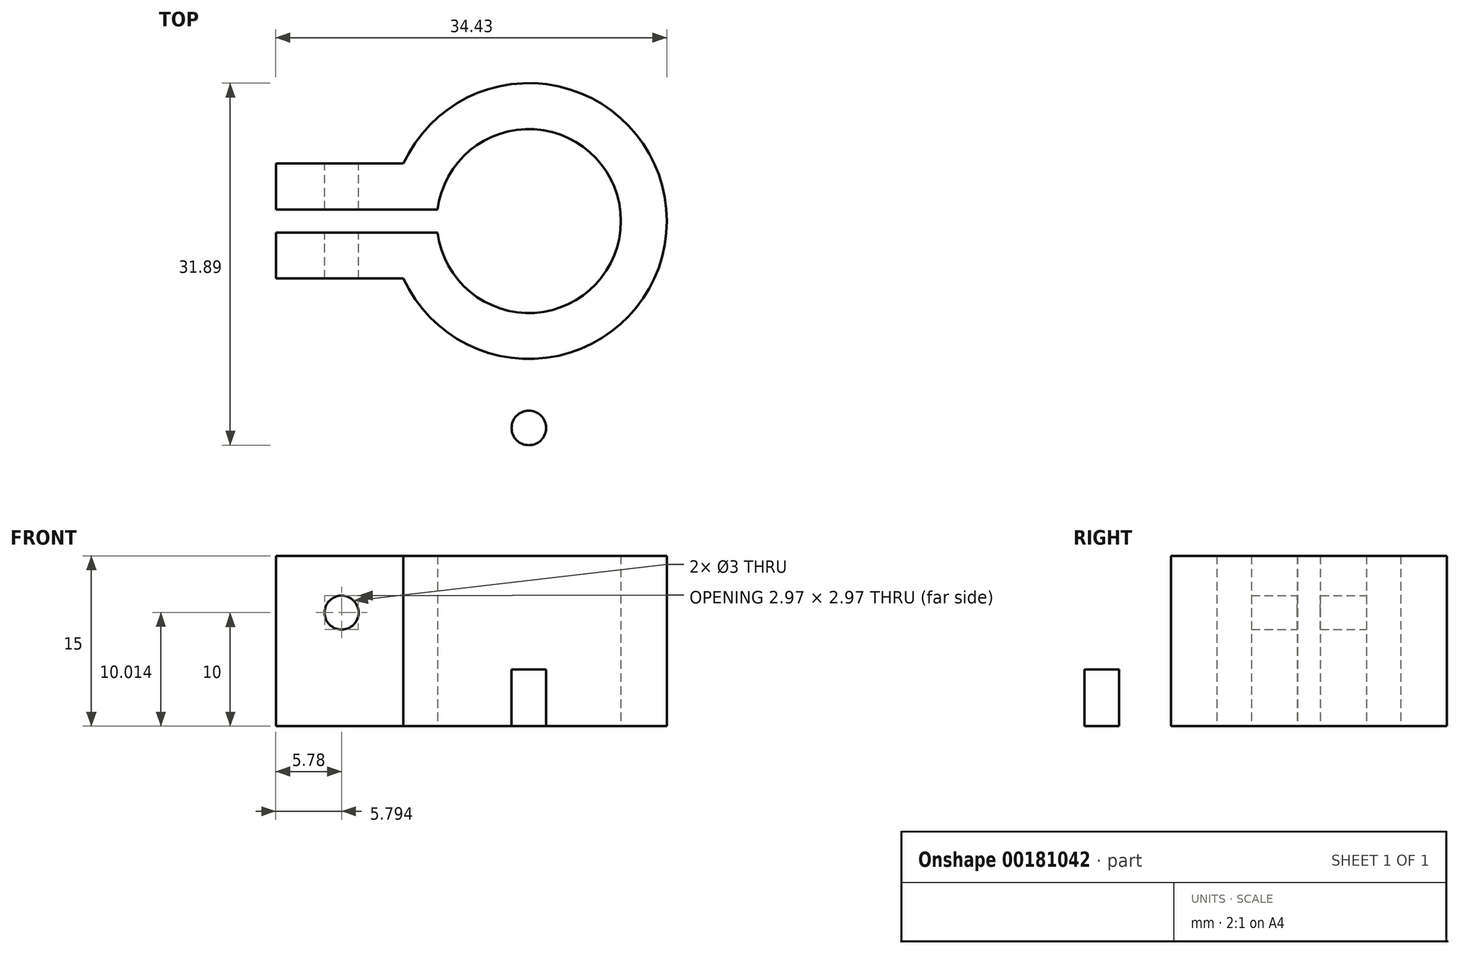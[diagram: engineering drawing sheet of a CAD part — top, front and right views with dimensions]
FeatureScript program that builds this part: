
annotation { "Feature Type Name" : "Feature", "Feature Type Description" : "" }
export const myFeature = defineFeature(function(context is Context, id is Id, definition is map)
    precondition{}
    {
        {
            var Q0;
            Q0=qCreatedBy(makeId("Top.planeOp"),FACE);
            var sketch = newSketch(context, id + "F0", { "sketchPlane" : qUnion([Q0])});
            skCircle(sketch, "E0", {"center": v(2.53, -18.82) * mm, "radius": 1.52 * mm});
            skArc(sketch, "E1", {"start": v(12.36, 17.85) * mm, "mid": v(2.53, 19.14) * mm, "end": v(-7.3, 17.85) * mm});
            skArc(sketch, "E2", {"start": v(-7.3, 17.85) * mm, "mid": v(-8.37, 16) * mm, "end": v(-6.51, 14.92) * mm});
            skArc(sketch, "E3", {"start": v(11.57, 14.92) * mm, "mid": v(2.53, 16.1) * mm, "end": v(-6.51, 14.92) * mm});
            skArc(sketch, "E4", {"start": v(11.57, 14.92) * mm, "mid": v(13.43, 16) * mm, "end": v(12.36, 17.85) * mm});
            skArc(sketch, "E5", {"start": v(2.53, -25.4) * mm, "mid": v(4.03, -25.28) * mm, "end": v(5.5, -24.95) * mm});
            skArc(sketch, "E6", {"start": v(5.5, -24.95) * mm, "mid": v(7.46, -24.21) * mm, "end": v(9.3, -23.2) * mm});
            skArc(sketch, "E7", {"start": v(9.3, -23.2) * mm, "mid": v(11.43, -21.63) * mm, "end": v(13.32, -19.78) * mm});
            skArc(sketch, "E8", {"start": v(13.32, -19.78) * mm, "mid": v(15.27, -17.24) * mm, "end": v(16.85, -14.46) * mm});
            skArc(sketch, "E9", {"start": v(16.85, -14.46) * mm, "mid": v(18.29, -10.8) * mm, "end": v(19.21, -6.98) * mm});
            skArc(sketch, "E10", {"start": v(19.21, -6.98) * mm, "mid": v(19.61, -3.8) * mm, "end": v(19.74, -0.6) * mm});
            skArc(sketch, "E11", {"start": v(-0.37, -24.97) * mm, "mid": v(1.06, -25.29) * mm, "end": v(2.53, -25.4) * mm});
            skArc(sketch, "E12", {"start": v(-4.1, -23.3) * mm, "mid": v(-2.3, -24.26) * mm, "end": v(-0.37, -24.97) * mm});
            skArc(sketch, "E13", {"start": v(-8.06, -20) * mm, "mid": v(-6.2, -21.78) * mm, "end": v(-4.1, -23.3) * mm});
            skArc(sketch, "E14", {"start": v(-11.57, -14.9) * mm, "mid": v(-10, -17.57) * mm, "end": v(-8.06, -20) * mm});
            skArc(sketch, "E15", {"start": v(-14.01, -7.73) * mm, "mid": v(-13.04, -11.4) * mm, "end": v(-11.57, -14.9) * mm});
            skArc(sketch, "E16", {"start": v(-14.67, -1.61) * mm, "mid": v(-14.47, -4.68) * mm, "end": v(-14.01, -7.73) * mm});
            skLineSegment(sketch, "E17", {"start": v(-14.68, 0.41) * mm, "end": v(-14.68, 16.58) * mm});
            skLineSegment(sketch, "E18", {"start": v(19.74, -0.6) * mm, "end": v(19.74, 16.58) * mm});
            skArc(sketch, "E19", {"start": v(13.98, 23.9) * mm, "mid": v(2.53, 25.4) * mm, "end": v(-8.92, 23.9) * mm});
            skArc(sketch, "E20", {"start": v(19.74, 16.18) * mm, "mid": v(18.2, 21.04) * mm, "end": v(13.98, 23.9) * mm});
            skArc(sketch, "E21", {"start": v(-8.92, 23.9) * mm, "mid": v(-13.14, 21.04) * mm, "end": v(-14.68, 16.19) * mm});
            skLineSegment(sketch, "E22", {"start": v(-5.57, 0.41) * mm, "end": v(-19.75, 0.41) * mm});
            skLineSegment(sketch, "E23", {"start": v(-19.75, -1.61) * mm, "end": v(-5.57, -1.61) * mm});
            skArc(sketch, "E24", {"start": v(-5.57, -1.61) * mm, "mid": v(-5.54, -1.61) * mm, "end": v(-5.5, -1.61) * mm});
            skArc(sketch, "E25", {"start": v(-5.5, 0.41) * mm, "mid": v(-5.54, 0.41) * mm, "end": v(-5.57, 0.41) * mm});
            skArc(sketch, "E26", {"start": v(-5.5, -1.61) * mm, "mid": v(10.63, -0.6) * mm, "end": v(-5.5, 0.41) * mm});
            skLineSegment(sketch, "E27", {"start": v(-19.75, 4.46) * mm, "end": v(-8.52, 4.46) * mm});
            skLineSegment(sketch, "E28", {"start": v(-19.75, -5.66) * mm, "end": v(-8.52, -5.66) * mm});
            skLineSegment(sketch, "E29", {"start": v(-19.75, -5.66) * mm, "end": v(-19.75, -1.61) * mm});
            skLineSegment(sketch, "E30", {"start": v(-19.75, 0.41) * mm, "end": v(-19.75, 4.46) * mm});
            skArc(sketch, "E31", {"start": v(-8.52, -5.66) * mm, "mid": v(14.68, -0.6) * mm, "end": v(-8.52, 4.46) * mm});
            skSolve(sketch);
        }
        {
            var Q0;
            {var subQ3=sQuery(id+"F0.wireOp",EDGE,"E24");Q0=makeQuery(id+"F0.imprint","IMPRINT",FACE,{"disambiguationData":[TD([[makeQuery(id+"F0.imprint","IMPRINT",EDGE,{"derivedFrom":subQ3}),-1.0]])]});}
            var Q1;
            {var subQ5=sQuery(id+"F0.wireOp",EDGE,"E30");Q1=makeQuery(id+"F0.imprint","IMPRINT",FACE,{"disambiguationData":[TD([[makeQuery(id+"F0.imprint","IMPRINT",EDGE,{"derivedFrom":subQ5}),-1.0]])]});}
            var Q2;
            {var subQ5=sQuery(id+"F0.wireOp",EDGE,"E29");Q2=makeQuery(id+"F0.imprint","IMPRINT",FACE,{"disambiguationData":[TD([[makeQuery(id+"F0.imprint","IMPRINT",EDGE,{"derivedFrom":subQ5}),-1.0]])]});}
            extrude(context, id + "F1", {"entities" : qUnion([Q0, Q1, Q2]), "depth" : 15 * mm});
        }
        {
            var Q0;
            Q0=makeQuery(id+"F0.imprint","IMPRINT",FACE,{"disambiguationData":[TD([[makeQuery(id+"F0.imprint","IMPRINT",EDGE,{"derivedFrom":sQuery(id+"F0.wireOp",EDGE,"E0")}),1.0]])]});
            var Q1;
            {var subQ3=sQuery(id+"F0.wireOp",EDGE,"E24");Q1=makeQuery(id+"F0.imprint","IMPRINT",FACE,{"disambiguationData":[TD([[makeQuery(id+"F0.imprint","IMPRINT",EDGE,{"derivedFrom":subQ3}),-1.0]])]});}
            extrude(context, id + "F2", {"entities" : qUnion([Q0, Q1]), "operationType" : NewBodyOperationType.ADD, "depth" : 5 * mm});
        }
        {
            var Q0;
            Q0=makeQuery(id+"F1.opExtrude","SWEPT_FACE",FACE,{"disambiguationData":[OSD([sQuery(id+"F0.wireOp",EDGE,"E27")])]});
            var sketch = newSketch(context, id + "F3", { "sketchPlane" : qUnion([Q0])});
            skPoint(sketch, "E32.endSnap0", {"position": v(19.75, 7.5) * mm});
            skPoint(sketch, "E33.endSnap0", {"position": v(15.38, 7.5) * mm});
            skCircle(sketch, "E34", {"center": v(13.96, 10) * mm, "radius": 1.5 * mm});
            skLineSegment(sketch, "E35", {"start": v(14.68, 5) * mm, "end": v(19.75, 5) * mm});
            skSolve(sketch);
        }
        {
            var Q0;
            Q0=makeQuery(id+"F3.imprint","IMPRINT",FACE,{"disambiguationData":[TD([[makeQuery(id+"F3.imprint","IMPRINT",EDGE,{"derivedFrom":sQuery(id+"F3.wireOp",EDGE,"E34")}),1.0]])]});
            extrude(context, id + "F4", {"entities" : qUnion([Q0]), "operationType" : NewBodyOperationType.REMOVE, "oppositeDirection" : true, "depth" : 25 * mm});
        }
    });
